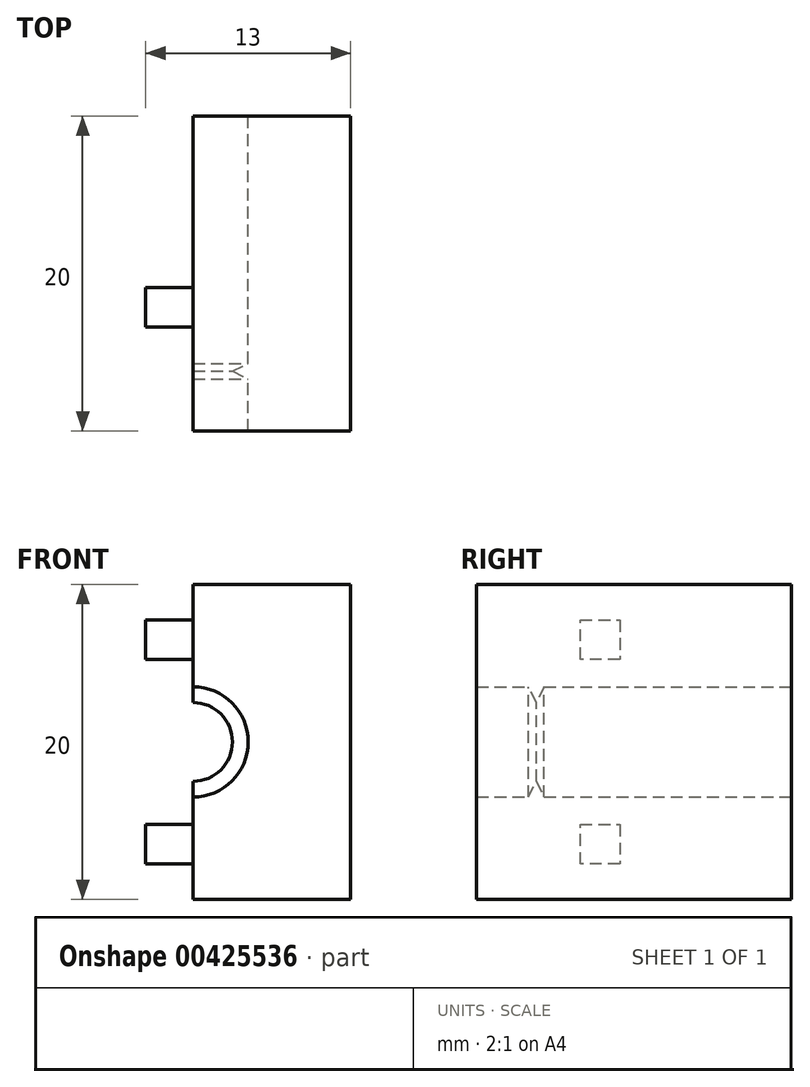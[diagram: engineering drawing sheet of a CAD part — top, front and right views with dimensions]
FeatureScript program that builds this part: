
annotation { "Feature Type Name" : "Feature", "Feature Type Description" : "" }
export const myFeature = defineFeature(function(context is Context, id is Id, definition is map)
    precondition{}
    {
        {
            var Q0;
            Q0=qCreatedBy(makeId("Front.planeOp"),FACE);
            var sketch = newSketch(context, id + "F0", { "sketchPlane" : qUnion([Q0])});
            skArc(sketch, "E0", {"start": v(0, 0) * mm, "mid": v(3.5, 3.5) * mm, "end": v(0, 7) * mm});
            skLineSegment(sketch, "E1", {"start": v(0, 7) * mm, "end": v(0, 0) * mm});
            skLineSegment(sketch, "E2", {"start": v(0, 13.5) * mm, "end": v(10, 13.5) * mm});
            skLineSegment(sketch, "E3", {"start": v(10, 13.5) * mm, "end": v(10, -6.5) * mm});
            skLineSegment(sketch, "E4", {"start": v(10, -6.5) * mm, "end": v(0, -6.5) * mm});
            skLineSegment(sketch, "E5", {"start": v(0, 13.5) * mm, "end": v(0, 7) * mm});
            skLineSegment(sketch, "E6", {"start": v(0, 0) * mm, "end": v(0, -6.5) * mm});
            skSolve(sketch);
        }
        {
            var Q0;
            Q0=makeQuery(id+"F0.imprint","IMPRINT",FACE,{"disambiguationData":[TD([[makeQuery(id+"F0.imprint","IMPRINT",EDGE,{"derivedFrom":sQuery(id+"F0.wireOp",EDGE,"E0")}),-1.0]])]});
            extrude(context, id + "F1", {"entities" : qUnion([Q0]), "depth" : 10 * mm});
        }
        {
            var Q0;
            Q0=qCreatedBy(makeId("Front.planeOp"),FACE);
            var sketch = newSketch(context, id + "F2", { "sketchPlane" : qUnion([Q0])});
            skArc(sketch, "E7", {"start": v(0, 1) * mm, "mid": v(2.5, 3.5) * mm, "end": v(0, 6) * mm});
            skLineSegment(sketch, "E8", {"start": v(0, 7) * mm, "end": v(0, 6) * mm});
            skLineSegment(sketch, "E9", {"start": v(0, 1) * mm, "end": v(0, 0) * mm});
            skArc(sketch, "E10", {"start": v(0, 0) * mm, "mid": v(3.5, 3.5) * mm, "end": v(0, 7) * mm});
            skSolve(sketch);
        }
        {
            var Q0;
            Q0=makeQuery(id+"F2.imprint","IMPRINT",FACE,{"disambiguationData":[TD([[makeQuery(id+"F2.imprint","IMPRINT",EDGE,{"derivedFrom":sQuery(id+"F2.wireOp",EDGE,"E7")}),-1.0]])]});
            extrude(context, id + "F3", {"entities" : qUnion([Q0]), "operationType" : NewBodyOperationType.ADD, "depth" : 6.7 * mm});
        }
        {
            var Q0;
            Q0=qCreatedBy(makeId("Front.planeOp"),FACE);
            var sketch = newSketch(context, id + "F4", { "sketchPlane" : qUnion([Q0])});
            skArc(sketch, "E11", {"start": v(0, 0) * mm, "mid": v(3.5, 3.5) * mm, "end": v(0, 7) * mm});
            skLineSegment(sketch, "E12", {"start": v(0, 7) * mm, "end": v(0, 6) * mm});
            skLineSegment(sketch, "E13", {"start": v(0, 0) * mm, "end": v(0, 1) * mm});
            skArc(sketch, "E14", {"start": v(0, 1) * mm, "mid": v(2.5, 3.5) * mm, "end": v(0, 6) * mm});
            skSolve(sketch);
        }
        {
            var Q0;
            Q0=makeQuery(id+"F4.imprint","IMPRINT",FACE,{"disambiguationData":[TD([[makeQuery(id+"F4.imprint","IMPRINT",EDGE,{"derivedFrom":sQuery(id+"F4.wireOp",EDGE,"E11")}),1.0]])]});
            extrude(context, id + "F5", {"entities" : qUnion([Q0]), "operationType" : NewBodyOperationType.REMOVE, "depth" : 5.7 * mm});
        }
        {
            var Q0;
            Q0=makeQuery(id+"F3.boolean.opBoolean","MERGE",FACE,{"derivedFrom":[makeQuery(id+"F1.opExtrude","SWEPT_FACE",FACE,{"disambiguationData":[OSD([sQuery(id+"F0.wireOp",EDGE,"E5")])]}),makeQuery(id+"F3.opExtrude","SWEPT_FACE",FACE,{"disambiguationData":[OSD([sQuery(id+"F2.wireOp",EDGE,"E8")])]})]});
            var sketch = newSketch(context, id + "F6", { "sketchPlane" : qUnion([Q0])});
            skLineSegment(sketch, "E15", {"start": v(5.7, 7) * mm, "end": v(6.2, 6) * mm});
            skLineSegment(sketch, "E16", {"start": v(6.2, 6) * mm, "end": v(6.7, 7) * mm});
            skLineSegment(sketch, "E17.0", {"start": v(5.7, 7) * mm, "end": v(5.7, 6) * mm});
            skLineSegment(sketch, "E18.0", {"start": v(6.7, 7) * mm, "end": v(6.7, 6) * mm});
            skLineSegment(sketch, "E19.0", {"start": v(6.7, 6) * mm, "end": v(5.7, 6) * mm});
            skSolve(sketch);
        }
        {
            var Q0;
            {var subQ0=sQuery(id+"F6.wireOp",EDGE,"E15");Q0=makeQuery(id+"F6.imprint","IMPRINT",FACE,{"disambiguationData":[TD([[makeQuery(id+"F6.imprint","IMPRINT",EDGE,{"derivedFrom":subQ0}),-1.0]])]});}
            var Q1;
            {var subQ0=sQuery(id+"F6.wireOp",EDGE,"E16");Q1=makeQuery(id+"F6.imprint","IMPRINT",FACE,{"disambiguationData":[TD([[makeQuery(id+"F6.imprint","IMPRINT",EDGE,{"derivedFrom":subQ0}),-1.0]])]});}
            var Q2;
            Q2=makeQuery(id+"F5.boolean.opBoolean","COPY",FACE,{"derivedFrom":makeQuery(id+"F5.opExtrude","SWEPT_FACE",FACE,{"disambiguationData":[OSD([sQuery(id+"F4.wireOp",EDGE,"E11")])]})});
            revolve(context, id + "F7", {"operationType" : NewBodyOperationType.REMOVE, "entities" : qUnion([Q0, Q1]), "axis" : qUnion([Q2]), "revolveType" : RevolveType.FULL, "oppositeDirection" : true});
        }
        {
            var Q0;
            Q0=makeQuery(id+"F6.imprint","IMPRINT",FACE,{"disambiguationData":[TD([[makeQuery(id+"F6.imprint","IMPRINT",EDGE,{"derivedFrom":sQuery(id+"F6.wireOp",EDGE,"E15")}),1.0]])]});
            var sketch = newSketch(context, id + "F8", { "sketchPlane" : qUnion([Q0])});
            skLineSegment(sketch, "E20", {"start": v(0.9, 11.25) * mm, "end": v(0.9, 8.75) * mm});
            skLineSegment(sketch, "E21", {"start": v(0.9, 8.75) * mm, "end": v(3.4, 8.75) * mm});
            skLineSegment(sketch, "E22", {"start": v(3.4, 8.75) * mm, "end": v(3.4, 11.25) * mm});
            skLineSegment(sketch, "E23", {"start": v(3.4, 11.25) * mm, "end": v(0.9, 11.25) * mm});
            skSolve(sketch);
        }
        {
            var Q0;
            Q0=makeQuery(id+"F3.boolean.opBoolean","MERGE",FACE,{"derivedFrom":[makeQuery(id+"F1.opExtrude","SWEPT_FACE",FACE,{"disambiguationData":[OSD([sQuery(id+"F0.wireOp",EDGE,"E6")])]}),makeQuery(id+"F3.opExtrude","SWEPT_FACE",FACE,{"disambiguationData":[OSD([sQuery(id+"F2.wireOp",EDGE,"E9")])]})]});
            var sketch = newSketch(context, id + "F9", { "sketchPlane" : qUnion([Q0])});
            skLineSegment(sketch, "E24", {"start": v(0.9, -1.75) * mm, "end": v(0.9, -4.25) * mm});
            skLineSegment(sketch, "E25", {"start": v(0.9, -4.25) * mm, "end": v(3.4, -4.25) * mm});
            skLineSegment(sketch, "E26", {"start": v(3.4, -4.25) * mm, "end": v(3.4, -1.75) * mm});
            skLineSegment(sketch, "E27", {"start": v(3.4, -1.75) * mm, "end": v(0.9, -1.75) * mm});
            skSolve(sketch);
        }
        {
            var Q0;
            Q0 = qSketchRegion(id + "F8", true);
            extrude(context, id + "F10", {"entities" : qUnion([Q0]), "operationType" : NewBodyOperationType.ADD, "depth" : 3 * mm});
        }
        {
            var Q0;
            Q0=makeQuery(id+"F9.imprint","IMPRINT",FACE,{"disambiguationData":[TD([[makeQuery(id+"F9.imprint","IMPRINT",EDGE,{"derivedFrom":sQuery(id+"F9.wireOp",EDGE,"E24")}),1.0]])]});
            extrude(context, id + "F11", {"entities" : qUnion([Q0]), "operationType" : NewBodyOperationType.ADD, "depth" : 3 * mm});
        }
        {
            var Q0;
            Q0=makeQuery(id+"F3.boolean.opBoolean","MERGE",FACE,{"derivedFrom":[makeQuery(id+"F1.opExtrude","SWEPT_FACE",FACE,{"disambiguationData":[OSD([sQuery(id+"F0.wireOp",EDGE,"E6")])]}),makeQuery(id+"F3.opExtrude","SWEPT_FACE",FACE,{"disambiguationData":[OSD([sQuery(id+"F2.wireOp",EDGE,"E9")])]})]});
            var sketch = newSketch(context, id + "F12", { "sketchPlane" : qUnion([Q0])});
            skLineSegment(sketch, "E28", {"start": v(0.65, -1.5) * mm, "end": v(0.65, -4.5) * mm});
            skLineSegment(sketch, "E29", {"start": v(0.65, -4.5) * mm, "end": v(3.65, -4.5) * mm});
            skLineSegment(sketch, "E30", {"start": v(3.65, -4.5) * mm, "end": v(3.65, -1.5) * mm});
            skLineSegment(sketch, "E31", {"start": v(3.65, -1.5) * mm, "end": v(0.65, -1.5) * mm});
            skSolve(sketch);
        }
        {
            var Q0;
            Q0 = qSketchRegion(id + "F0", true);
            extrude(context, id + "F13", {"entities" : qUnion([Q0]), "operationType" : NewBodyOperationType.ADD, "oppositeDirection" : true, "depth" : 10 * mm});
        }
        {
            var Q0;
            Q0=makeQuery(id+"F13.opExtrude","CAP_FACE",FACE,{"disambiguationData":[OSD([sQuery(id+"F0.wireOp",EDGE,"E1"),sQuery(id+"F0.wireOp",EDGE,"E2"),sQuery(id+"F0.wireOp",EDGE,"E3"),sQuery(id+"F0.wireOp",EDGE,"E4"),sQuery(id+"F0.wireOp",EDGE,"E5"),sQuery(id+"F0.wireOp",EDGE,"E6")])],"isStart":true});
            extrude(context, id + "F14", {"entities" : qUnion([Q0]), "operationType" : NewBodyOperationType.REMOVE, "oppositeDirection" : true, "depth" : 11 * mm});
        }
    });
